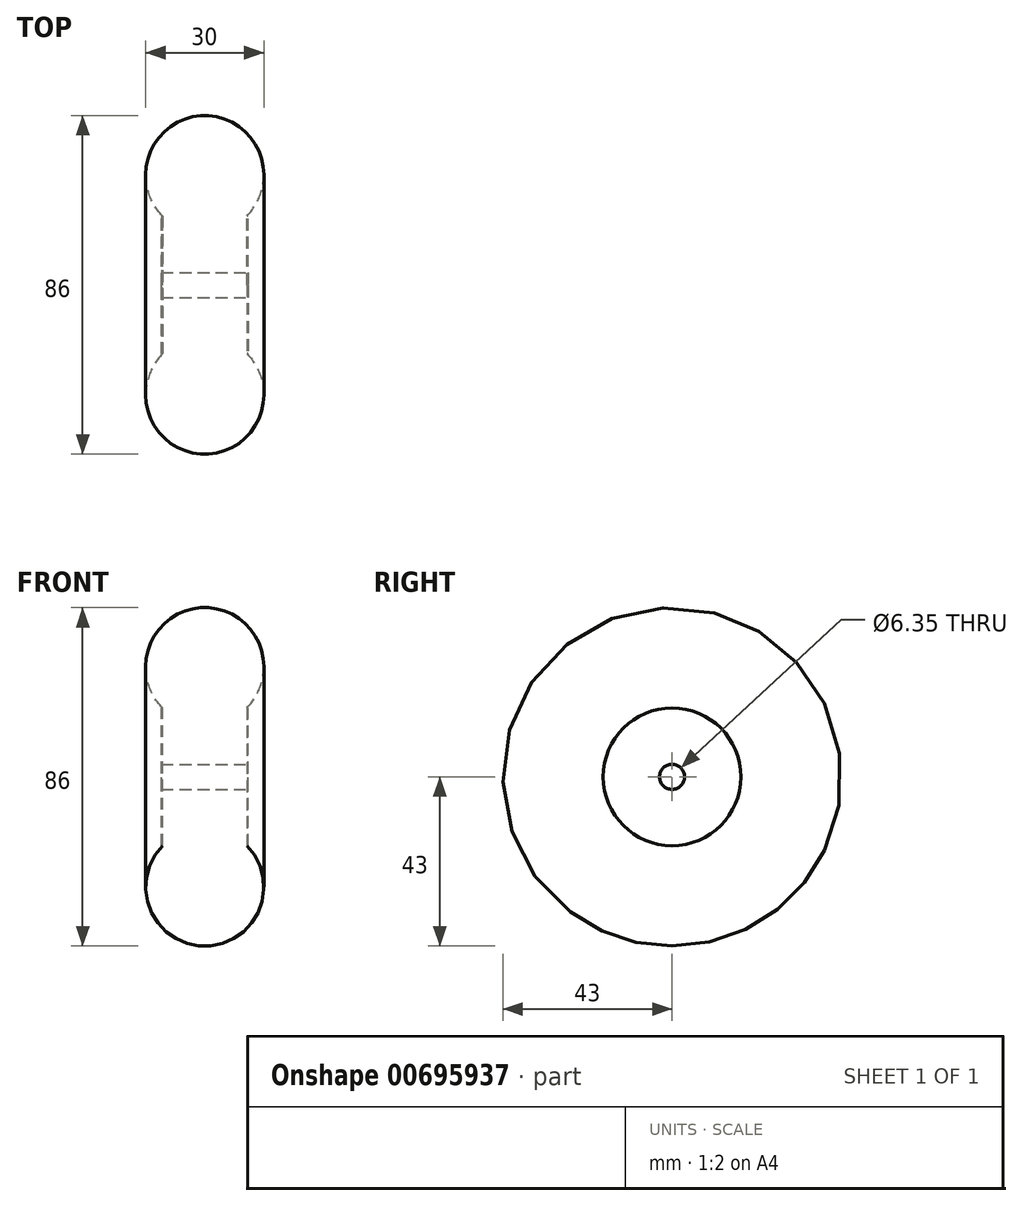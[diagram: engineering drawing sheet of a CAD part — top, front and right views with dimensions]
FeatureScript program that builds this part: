
annotation { "Feature Type Name" : "Feature", "Feature Type Description" : "" }
export const myFeature = defineFeature(function(context is Context, id is Id, definition is map)
    precondition{}
    {
        {
            var Q0;
            Q0=qCreatedBy(makeId("Right.planeOp"),FACE);
            var sketch = newSketch(context, id + "F0", { "sketchPlane" : qUnion([Q0])});
            skCircle(sketch, "E0", {"center": v(0, 0) * mm, "radius": 17.5 * mm});
            skSolve(sketch);
        }
        {
            var Q0;
            Q0 = qSketchRegion(id + "F0", true);
            extrude(context, id + "F1", {"entities" : qUnion([Q0]), "endBound" : BoundingType.SYMMETRIC, "depth" : 22 * mm, "offsetDistance" : 25 * mm});
        }
        {
            var Q0;
            Q0=qCreatedBy(makeId("Right.planeOp"),FACE);
            var sketch = newSketch(context, id + "F2", { "sketchPlane" : qUnion([Q0])});
            skCircle(sketch, "E1", {"center": v(0, 0) * mm, "radius": 28 * mm});
            skSolve(sketch);
        }
        {
            var Q0;
            Q0=qCreatedBy(makeId("Front.planeOp"),FACE);
            var sketch = newSketch(context, id + "F3", { "sketchPlane" : qUnion([Q0])});
            skCircle(sketch, "E2", {"center": v(0, -28) * mm, "radius": 15 * mm});
            skSolve(sketch);
        }
        {
            var Q0;
            Q0=makeQuery(id+"F3.imprint","IMPRINT",FACE,{"disambiguationData":[TD([[makeQuery(id+"F3.imprint","IMPRINT",EDGE,{"derivedFrom":sQuery(id+"F3.wireOp",EDGE,"E2")}),1.0]])]});
            var Q1;
            Q1=sQuery(id+"F2.wireOp",EDGE,"E1");
            sweep(context, id + "F4", {"operationType" : NewBodyOperationType.ADD, "profiles" : qUnion([Q0]), "path" : qUnion([Q1])});
        }
        {
            var Q0;
            Q0=makeQuery(id+"F1.opExtrude","CAP_FACE",FACE,{"disambiguationData":[OSD([sQuery(id+"F0.wireOp",EDGE,"E0")])],"isStart":false});
            var sketch = newSketch(context, id + "F5", { "sketchPlane" : qUnion([Q0])});
            skCircle(sketch, "E3", {"center": v(0, 0) * mm, "radius": 3.18 * mm});
            skSolve(sketch);
        }
        {
            var Q0;
            Q0 = qSketchRegion(id + "F5", true);
            extrude(context, id + "F6", {"entities" : qUnion([Q0]), "operationType" : NewBodyOperationType.REMOVE, "endBound" : BoundingType.THROUGH_ALL, "oppositeDirection" : true, "depth" : 25 * mm, "offsetDistance" : 25 * mm});
        }
    });
